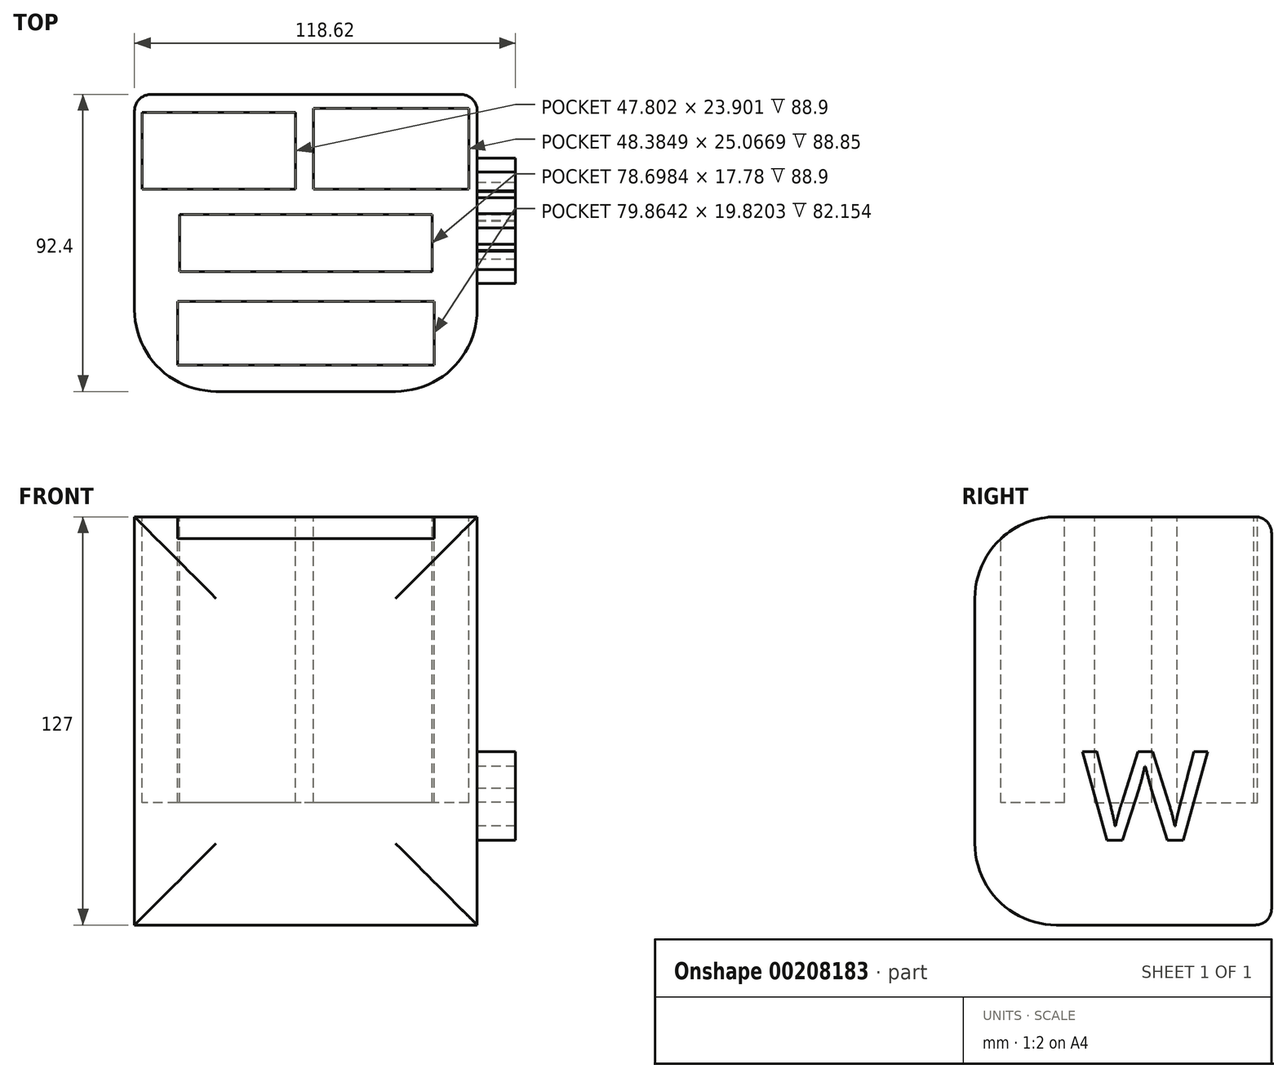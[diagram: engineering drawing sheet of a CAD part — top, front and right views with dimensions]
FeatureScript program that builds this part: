
annotation { "Feature Type Name" : "Feature", "Feature Type Description" : "" }
export const myFeature = defineFeature(function(context is Context, id is Id, definition is map)
    precondition{}
    {
        {
            var Q0;
            Q0=qCreatedBy(makeId("Top.planeOp"),FACE);
            var sketch = newSketch(context, id + "F0", { "sketchPlane" : qUnion([Q0])});
            skLineSegment(sketch, "E0.bottom", {"start": v(53.34, -46.2) * mm, "end": v(-53.34, -46.2) * mm});
            skLineSegment(sketch, "E0.top", {"start": v(53.34, 46.2) * mm, "end": v(-53.34, 46.2) * mm});
            skLineSegment(sketch, "E0.left", {"start": v(53.34, -46.2) * mm, "end": v(53.34, 46.2) * mm});
            skLineSegment(sketch, "E0.right", {"start": v(-53.34, -46.2) * mm, "end": v(-53.34, 46.2) * mm});
            skPoint(sketch, "E0.middle", {"position": v(0, 0) * mm});
            skSolve(sketch);
        }
        {
            var Q0;
            Q0 = qSketchRegion(id + "F0", true);
            extrude(context, id + "F1", {"entities" : qUnion([Q0]), "depth" : 127 * mm});
        }
        {
            var Q0;
            Q0=makeQuery(id+"F1.opExtrude","CAP_FACE",FACE,{"disambiguationData":[OSD([sQuery(id+"F0.wireOp",EDGE,"E0.bottom"),sQuery(id+"F0.wireOp",EDGE,"E0.top"),sQuery(id+"F0.wireOp",EDGE,"E0.left"),sQuery(id+"F0.wireOp",EDGE,"E0.right")])],"isStart":false});
            var sketch = newSketch(context, id + "F2", { "sketchPlane" : qUnion([Q0])});
            skLineSegment(sketch, "E1.bottom", {"start": v(-3.2, 16.76) * mm, "end": v(-51, 16.76) * mm});
            skLineSegment(sketch, "E1.top", {"start": v(-3.2, 40.66) * mm, "end": v(-51, 40.66) * mm});
            skLineSegment(sketch, "E1.left", {"start": v(-3.2, 16.76) * mm, "end": v(-3.2, 40.66) * mm});
            skLineSegment(sketch, "E1.right", {"start": v(-51, 16.76) * mm, "end": v(-51, 40.66) * mm});
            skPoint(sketch, "E1.middle", {"position": v(-27.1, 28.71) * mm});
            skLineSegment(sketch, "E2.bottom", {"start": v(50.72, 16.76) * mm, "end": v(2.33, 16.76) * mm});
            skLineSegment(sketch, "E2.top", {"start": v(50.72, 41.83) * mm, "end": v(2.33, 41.83) * mm});
            skLineSegment(sketch, "E2.left", {"start": v(50.72, 16.76) * mm, "end": v(50.72, 41.83) * mm});
            skLineSegment(sketch, "E2.right", {"start": v(2.33, 16.76) * mm, "end": v(2.33, 41.83) * mm});
            skPoint(sketch, "E2.middle", {"position": v(26.52, 29.3) * mm});
            skLineSegment(sketch, "E3.bottom", {"start": v(39.35, -8.9) * mm, "end": v(-39.35, -8.9) * mm});
            skLineSegment(sketch, "E3.top", {"start": v(39.35, 8.9) * mm, "end": v(-39.35, 8.9) * mm});
            skLineSegment(sketch, "E3.left", {"start": v(39.35, -8.9) * mm, "end": v(39.35, 8.9) * mm});
            skLineSegment(sketch, "E3.right", {"start": v(-39.35, -8.9) * mm, "end": v(-39.35, 8.9) * mm});
            skPoint(sketch, "E3.middle", {"position": v(0, 0) * mm});
            skLineSegment(sketch, "E4.bottom", {"start": v(39.93, -18.22) * mm, "end": v(-39.93, -18.22) * mm});
            skLineSegment(sketch, "E4.top", {"start": v(39.93, -38.04) * mm, "end": v(-39.93, -38.04) * mm});
            skLineSegment(sketch, "E4.left", {"start": v(39.93, -18.22) * mm, "end": v(39.93, -38.04) * mm});
            skLineSegment(sketch, "E4.right", {"start": v(-39.93, -18.22) * mm, "end": v(-39.93, -38.04) * mm});
            skPoint(sketch, "E4.middle", {"position": v(0, -28.13) * mm});
            skSolve(sketch);
        }
        {
            var Q0;
            Q0=makeQuery(id+"F2.imprint","IMPRINT",FACE,{"disambiguationData":[TD([[makeQuery(id+"F2.imprint","IMPRINT",EDGE,{"derivedFrom":sQuery(id+"F2.wireOp",EDGE,"E1.bottom")}),-1.0]])]});
            var Q1;
            Q1=makeQuery(id+"F2.imprint","IMPRINT",FACE,{"disambiguationData":[TD([[makeQuery(id+"F2.imprint","IMPRINT",EDGE,{"derivedFrom":sQuery(id+"F2.wireOp",EDGE,"E2.bottom")}),-1.0]])]});
            var Q2;
            Q2=makeQuery(id+"F2.imprint","IMPRINT",FACE,{"disambiguationData":[TD([[makeQuery(id+"F2.imprint","IMPRINT",EDGE,{"derivedFrom":sQuery(id+"F2.wireOp",EDGE,"E3.bottom")}),-1.0]])]});
            var Q3;
            Q3=makeQuery(id+"F2.imprint","IMPRINT",FACE,{"disambiguationData":[TD([[makeQuery(id+"F2.imprint","IMPRINT",EDGE,{"derivedFrom":sQuery(id+"F2.wireOp",EDGE,"E4.bottom")}),1.0]])]});
            var Q4;
            Q4 = qSketchRegion(id + "F2", true);
            extrude(context, id + "F3", {"entities" : qUnion([Q0, Q1, Q2, Q3, Q4]), "operationType" : NewBodyOperationType.REMOVE, "oppositeDirection" : true, "depth" : 88.9 * mm});
        }
        {
            var Q0;
            Q0=makeQuery(id+"F1.opExtrude","SWEPT_FACE",FACE,{"disambiguationData":[OSD([sQuery(id+"F0.wireOp",EDGE,"E0.bottom")])]});
            fillet(context, id + "F4", {"entities" : qUnion([Q0]), "radius" : 25.4 * mm, "tangentPropagation" : true, "allowEdgeOverflow" : false});
        }
        {
            var Q0;
            Q0=makeQuery(id+"F1.opExtrude","SWEPT_FACE",FACE,{"disambiguationData":[OSD([sQuery(id+"F0.wireOp",EDGE,"E0.top")])]});
            fillet(context, id + "F5", {"entities" : qUnion([Q0]), "radius" : 5.08 * mm, "tangentPropagation" : true, "allowEdgeOverflow" : false});
        }
        {
            var Q0;
            Q0=makeQuery(id+"F1.opExtrude","SWEPT_FACE",FACE,{"disambiguationData":[OSD([sQuery(id+"F0.wireOp",EDGE,"E0.left")])]});
            var sketch = newSketch(context, id + "F6", { "sketchPlane" : qUnion([Q0])});
            skText(sketch, "E5", { "text": "w", "fontName": "OpenSans-Regular.ttf"});
            skPoint(sketch, "E5.firstSnap0", {"position": v(-20.8, 63.5) * mm});
            const initialGuessF6  = {"E5": [-0.01321, 0.02637, 1, 0, 0.03713]};
            skSetInitialGuess(sketch, initialGuessF6);
            skSolve(sketch);
        }
        {
            var Q0;
            Q0 = qSketchRegion(id + "F6", true);
            extrude(context, id + "F7", {"entities" : qUnion([Q0]), "operationType" : NewBodyOperationType.ADD, "depth" : 11.94 * mm});
        }
    });
